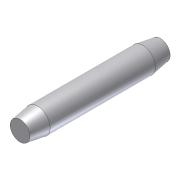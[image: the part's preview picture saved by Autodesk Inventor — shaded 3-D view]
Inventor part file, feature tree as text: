
AUTODESK INVENTOR PART (.ipt)
format: ipt  version: 2012 (Build 160160000, 160)  size: 77,312 bytes
history: native  units: in
note: dims shown in document units (in); Inventor stores cm internally (conversion verified against a paired STEP export)
features: chamfer x2, extrude x1, sketch x1
ambient origin geometry x8: Origin, YZ Plane, XZ Plane, XY Plane, X Axis, Y Axis, Z Axis, Center Point
bodies: Solid1 (feature_tree)
feature tree (4):
  extrude  "Extrusion1"  Depth=8.0in TaperAngle=0.0deg
  chamfer  "Chamfer1"  Distance=0.1562in Angle=45.0deg
  chamfer  "Chamfer2"  Distance=1.0in Angle=45.0deg
  sketch  "Sketch1"  dims[d0=1.4375in d1=8.0in d2=0.0in d3=0.1562in d4=1.0in d5=45.0deg d6=1.0in d7=0.1562in d8=45.0deg]
